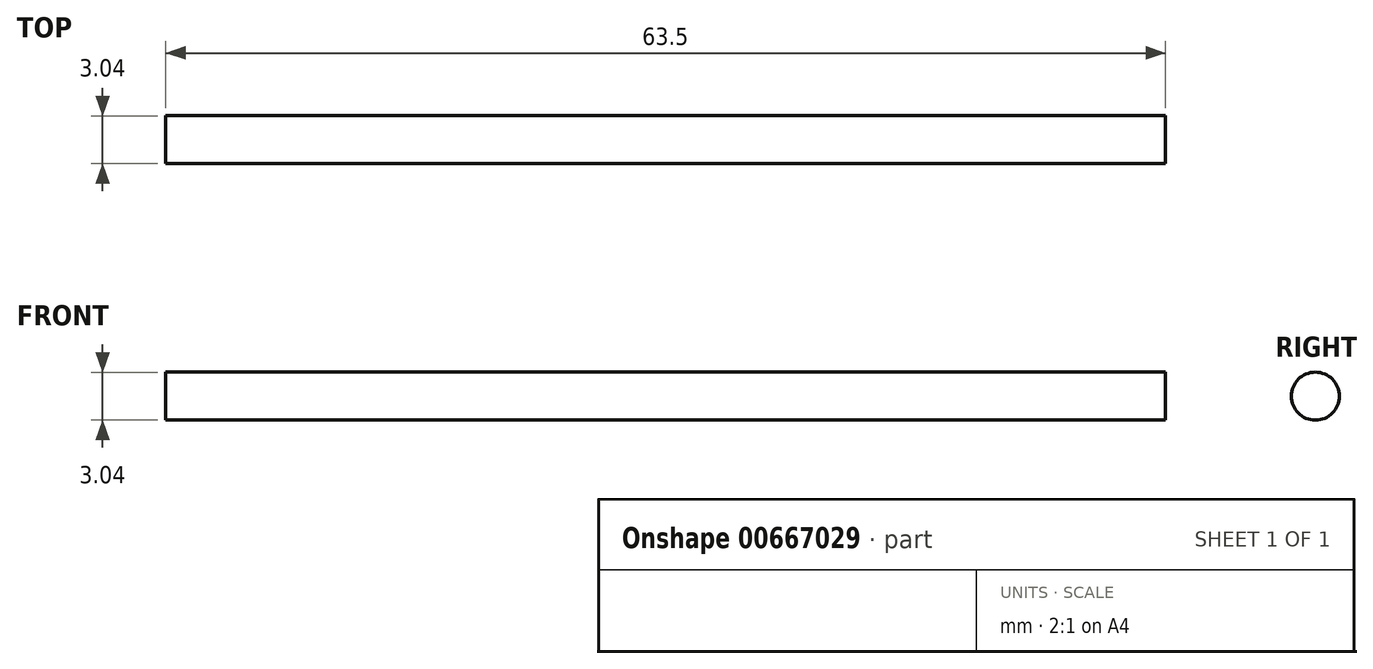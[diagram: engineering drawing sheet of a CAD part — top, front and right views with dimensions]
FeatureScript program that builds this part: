
annotation { "Feature Type Name" : "Feature", "Feature Type Description" : "" }
export const myFeature = defineFeature(function(context is Context, id is Id, definition is map)
    precondition{}
    {
        {
            var Q0;
            Q0=qCreatedBy(makeId("Right.planeOp"),FACE);
            var sketch = newSketch(context, id + "F0", { "sketchPlane" : qUnion([Q0])});
            skCircle(sketch, "E0", {"center": v(0, 0) * mm, "radius": 1.52 * mm});
            skSolve(sketch);
        }
        {
            var Q0;
            Q0=makeQuery(id+"F0.imprint","IMPRINT",FACE,{"disambiguationData":[TD([[makeQuery(id+"F0.imprint","IMPRINT",EDGE,{"derivedFrom":sQuery(id+"F0.wireOp",EDGE,"E0")}),1.0]])]});
            extrude(context, id + "F1", {"entities" : qUnion([Q0]), "depth" : 63.5 * mm, "offsetDistance" : 25.4 * mm});
        }
    });
